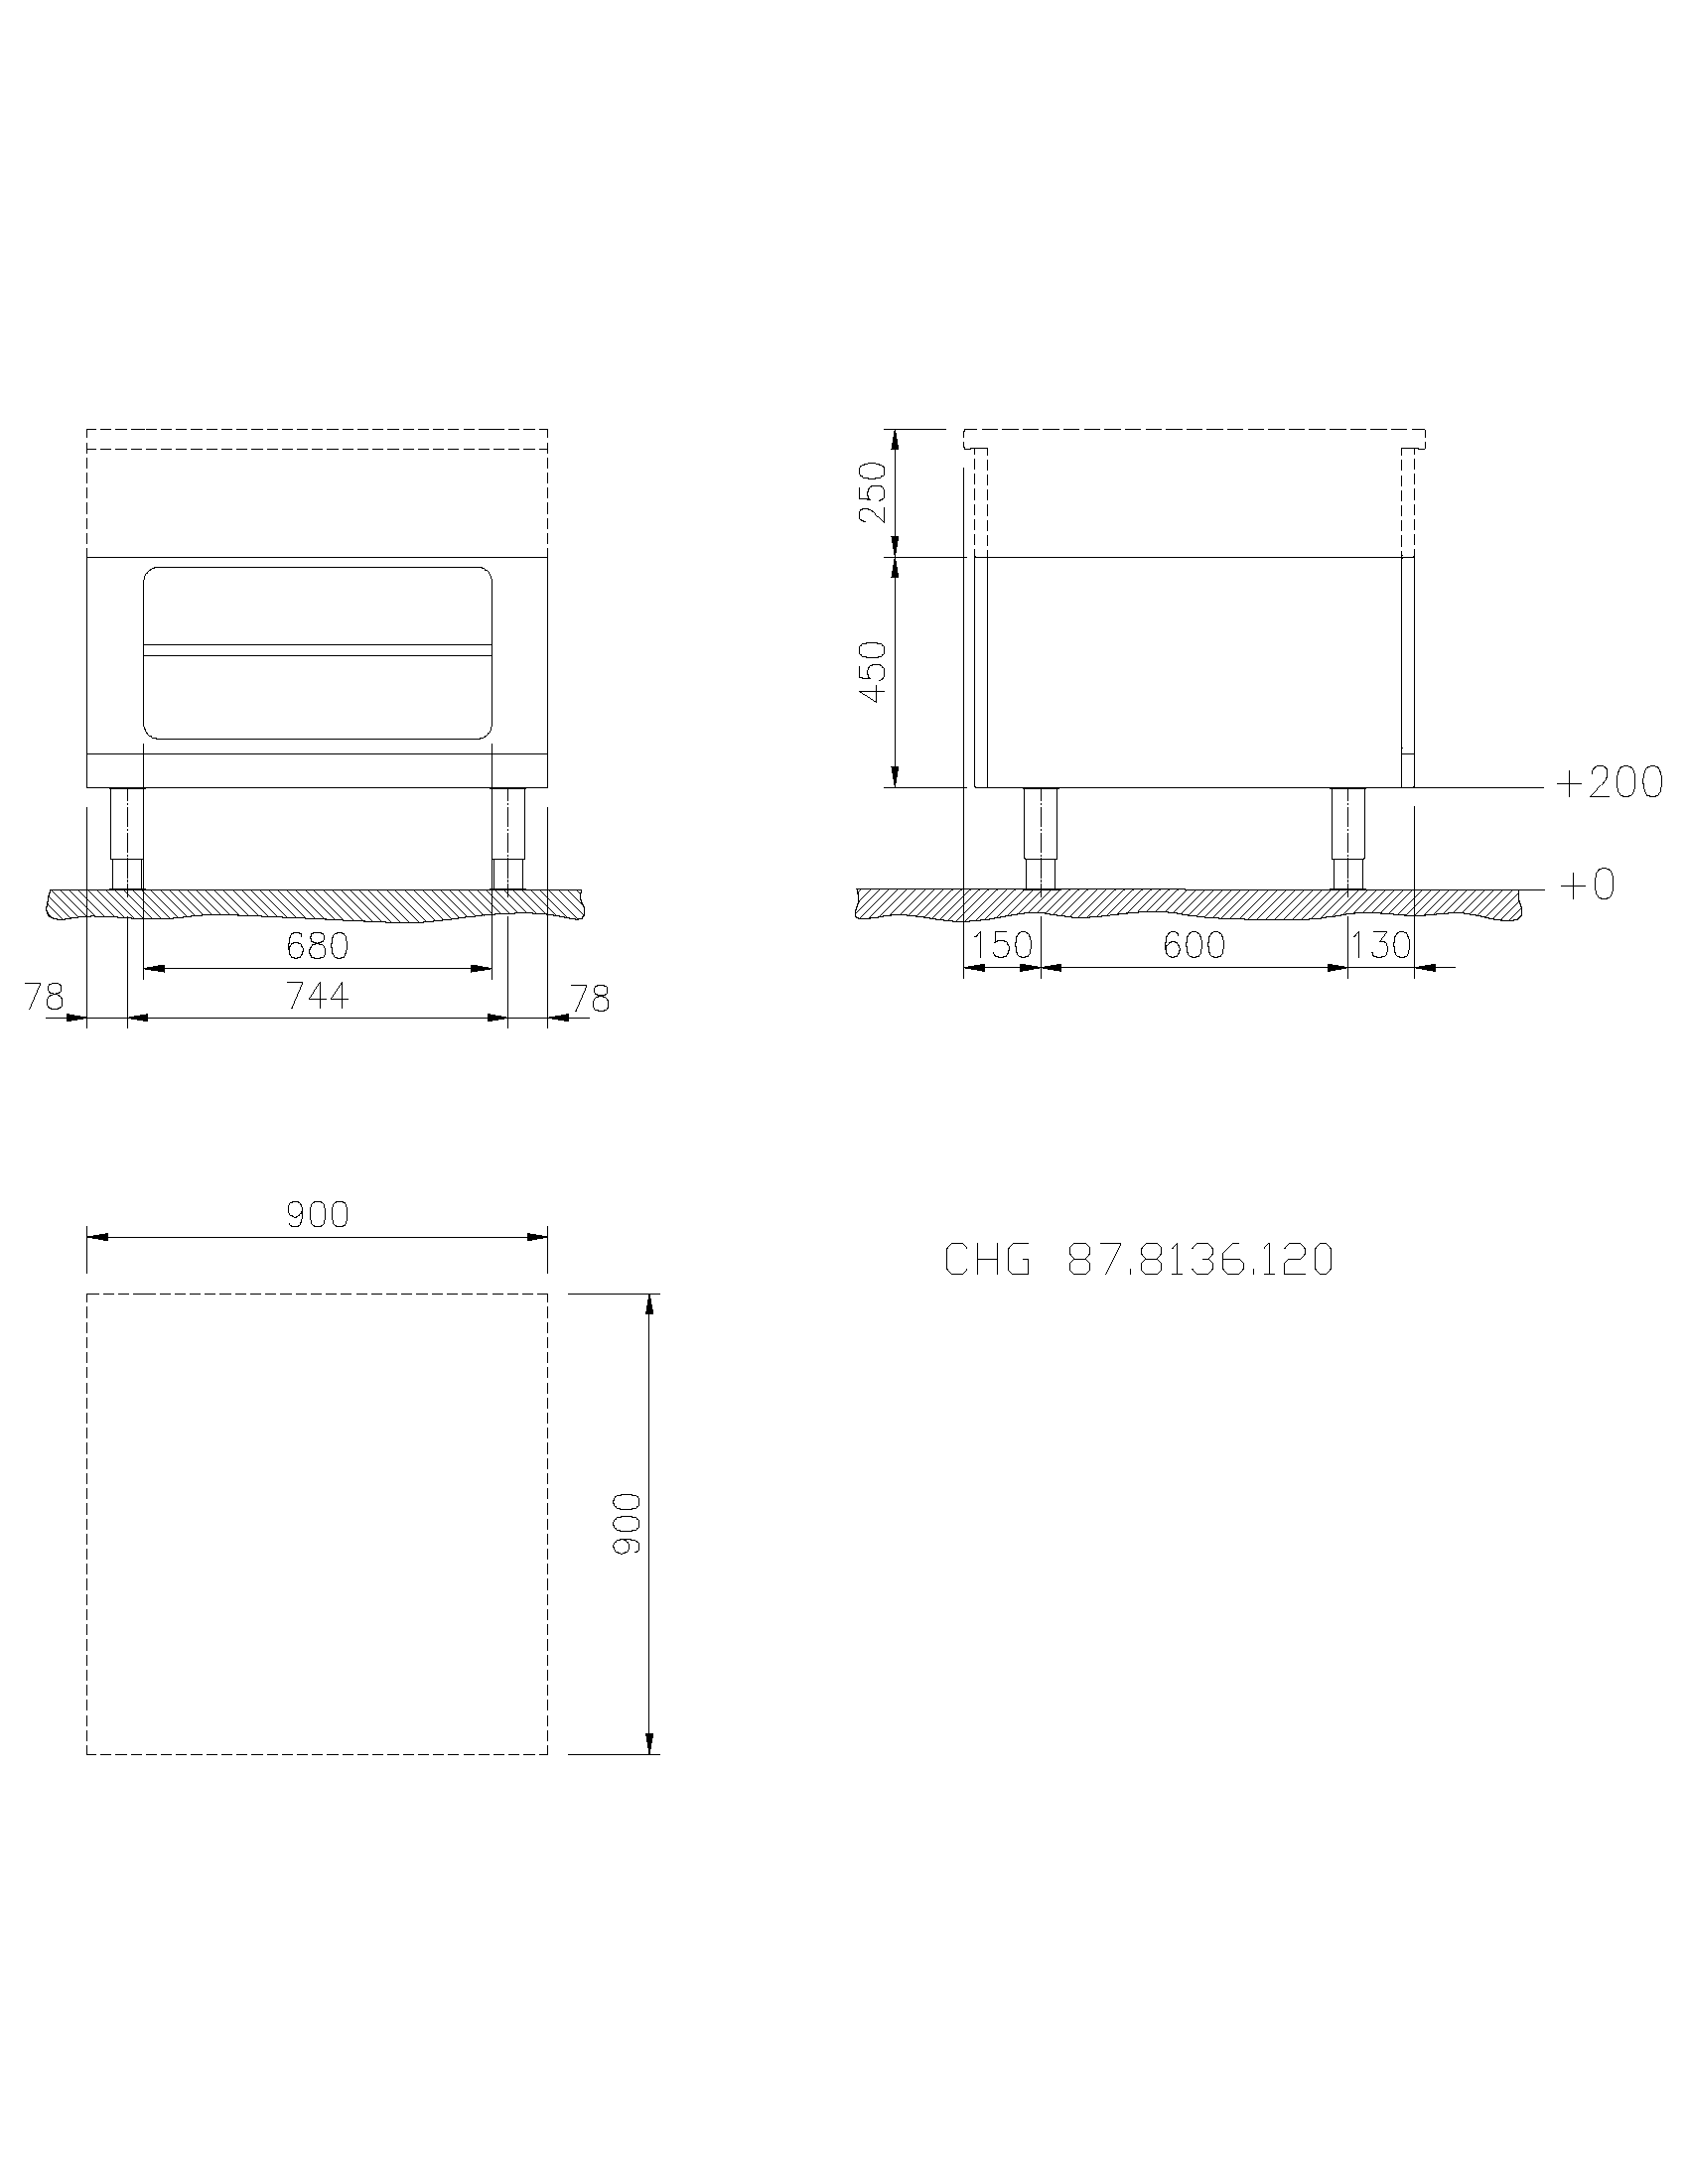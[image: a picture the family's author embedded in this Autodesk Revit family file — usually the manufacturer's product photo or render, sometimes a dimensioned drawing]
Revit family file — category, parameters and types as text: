
# Revit family: QF_ELECTROLUXPROFESSIONAL_589807_MC1HCAGOOM
name_source: partatom
category: Attrezzature speciali
units: mm (PartAtom-declared; Revit-internal decimal feet)

## family parameters
Basato su piano di lavoro = No
Condiviso = No
Punto di calcolo locali = No
Quota connettore circolare = Usa diametro
Sempre verticale = Sì
Taglio con vuoti quando caricato = No
Tipo di parte = Normale

## types (1)
- Standard
    Accessory = Sì
    Cold Water Size = 0"
    Compressed Air Pressure = 0.00 psi
    Compressed Air Size = 0"
    Compressed Air Volume = 0 GPM
    Condensate Return Size = 0"
    Cycle = 0 Hz
    Depth Actual = 900 mm  [stored 2.95276 ft]
    Descrizione = OPEN BASE,H3,GN,1S,700X900X450 MARINE
    Direct Waste Size = 0"
    Gas Input Pressure = 0.0
    Gas KW = 0
    Gas Size = 0"
    HP = 0 HP
    Height Actual = 450 mm  [stored 1.47638 ft]
    Hot Water Size = 0"
    Item Number = 589807
    Length Actual = 700 mm  [stored 2.29659 ft]
    Modello = MC1HCAGOOM
    Phase = 0
    Produttore = Electrolux Professional
    Prospetto di default = 0 mm  [stored 0 ft]
    Refrigerant Compressor Remote = Sì
    Refrigeration Liquid Line Size = 0 mm  [stored 0 ft]
    Refrigeration Suction Line Size = 0 mm  [stored 0 ft]
    Steam Consumption per Hour = 0
    Steam Supply Maximum Pressure = 0.00 psi
    Steam Supply Minimum Pressure = 0.00 psi
    Steam Supply Size = 0"
    URL = https://www.electroluxprofessional.com
    URL Manufacturer = https://www.electroluxprofessional.com
    Volts = 0 V
    Watts = 0 W
    Weight = 21.00 kg

note: source unit labels omitted for Gas Input Pressure — the stored unit's dimension contradicts the parameter name (converter mislabeling)

note: [stored X ft] marks values corroborated as IEEE doubles in the binary element streams (Revit-internal decimal feet)

## geometry (parser evidence)
native form markers: Blend x10, Sweep x3
no freeform markers — native parametric forms only
